# Revit family: Square-Table-Tops_Lamboo
name_source: partatom
category: Casework
units: mm (PartAtom-declared; Revit-internal decimal feet)

## family parameters
Always vertical = Yes
Cut with Voids When Loaded = Yes
Room Calculation Point = No
Shared = No
Work Plane-Based = Yes

## types (12) — shared parameters
Keynote = 07 42 23
Manufacturer = Lamboo® Technologies™
Model = Lamboo Table Tops
Product Documentation Link = https://www.arcat.com
Specification = https://www.arcat.com
URL = https://www.lamboo.us
zero-valued in all types: Default Elevation, Depth

## per-type parameters (varying)
| type | Height | Thickness | Width |
| VCP(075)-INT-4848 | 47.5 " | 0.75 " | 47.5 " |
| VCP(100)-INT-4848 | 47.5 " | 1 " | 47.5 " |
| VCP(150)-INT-4848 | 47.5 " | 1.5 " | 47.5 " |
| VCP(075)-INT-2424 | 23.5 " | 0.75 " | 23.5 " |
| VCP(150)-INT-2424 | 23.5 " | 1.5 " | 23.5 " |
| VCP(100)-INT-2424 | 23.5 " | 1 " | 23.5 " |
| VCP(075)-INT-3030 | 29.75 " | 0.75 " | 29.75 " |
| VCP(100)-INT-3030 | 29.75 " | 1 " | 29.75 " |
| VCP(150)-INT-3030 | 29.75 " | 1.5 " | 29.75 " |
| VCP(075)-INT-3636 | 35.5 " | 0.75 " | 35.5 " |
| VCP(150)-INT-3636 | 35.5 " | 1.5 " | 35.5 " |
| VCP(100)-INT-3636 | 35.5 " | 1 " | 35.5 " |

## geometry (parser evidence)
native form markers: Sweep x1
no freeform markers — native parametric forms only
